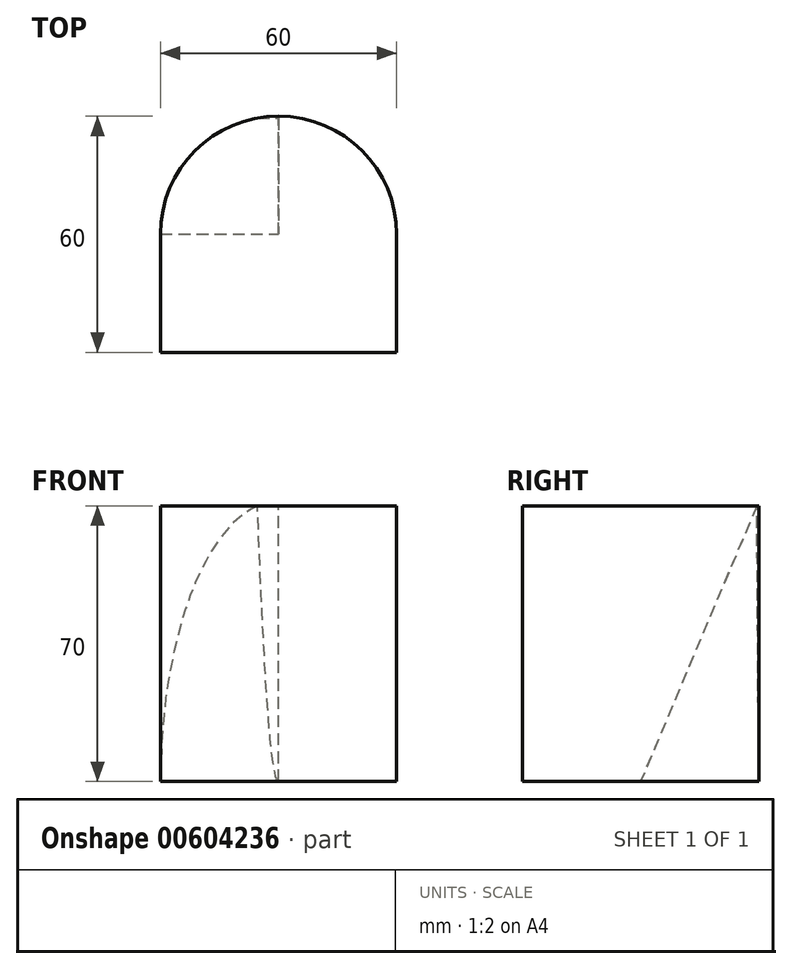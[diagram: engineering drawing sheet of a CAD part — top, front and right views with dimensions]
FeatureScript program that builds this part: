
annotation { "Feature Type Name" : "Feature", "Feature Type Description" : "" }
export const myFeature = defineFeature(function(context is Context, id is Id, definition is map)
    precondition{}
    {
        {
            var Q0;
            Q0=qCreatedBy(makeId("Top.planeOp"),FACE);
            var sketch = newSketch(context, id + "F0", { "sketchPlane" : qUnion([Q0])});
            skLineSegment(sketch, "E0.bottom", {"start": v(-30, 30) * mm, "end": v(30, 30) * mm});
            skLineSegment(sketch, "E0.top", {"start": v(-30, -30) * mm, "end": v(30, -30) * mm});
            skLineSegment(sketch, "E0.left", {"start": v(-30, 30) * mm, "end": v(-30, -30) * mm});
            skLineSegment(sketch, "E0.right", {"start": v(30, 30) * mm, "end": v(30, -30) * mm});
            skPoint(sketch, "E0.middle", {"position": v(0, 0) * mm});
            skSolve(sketch);
        }
        {
            var Q0;
            Q0=makeQuery(id+"F0.imprint","IMPRINT",FACE,{"disambiguationData":[TD([[makeQuery(id+"F0.imprint","IMPRINT",EDGE,{"derivedFrom":sQuery(id+"F0.wireOp",EDGE,"E0.bottom")}),-1.0]])]});
            extrude(context, id + "F1", {"entities" : qUnion([Q0]), "depth" : 70 * mm, "offsetDistance" : 25 * mm});
        }
        {
            var Q0;
            Q0=makeQuery(id+"F1.opExtrude","CAP_FACE",FACE,{"disambiguationData":[OSD([sQuery(id+"F0.wireOp",EDGE,"E0.bottom"),sQuery(id+"F0.wireOp",EDGE,"E0.top"),sQuery(id+"F0.wireOp",EDGE,"E0.left"),sQuery(id+"F0.wireOp",EDGE,"E0.right")])],"isStart":false});
            var sketch = newSketch(context, id + "F2", { "sketchPlane" : qUnion([Q0])});
            skCircle(sketch, "E1", {"center": v(0, 0) * mm, "radius": 30 * mm});
            skSolve(sketch);
        }
        {
            var Q0;
            {var subQ0=sQuery(id+"F2.wireOp",EDGE,"E1");var subQ1=makeQuery(id+"F1.opExtrude","CAP_EDGE",EDGE,{"disambiguationData":[OSD([sQuery(id+"F0.wireOp",EDGE,"E0.bottom")])],"isStart":false});var subQ2=makeQuery(id+"F2.imprint","INTERSECT",VERTEX,{"derivedFrom":[subQ1,subQ0]});Q0=makeQuery(id+"F2.imprint","IMPRINT",FACE,{"disambiguationData":[TD([[makeQuery(id+"F2.imprint","IMPRINT",EDGE,{"disambiguationData":[TD([[subQ2,-1.0]])],"derivedFrom":subQ0}),-1.0]])]});}
            var Q1;
            {var subQ0=sQuery(id+"F2.wireOp",EDGE,"E1");var subQ1=makeQuery(id+"F1.opExtrude","CAP_EDGE",EDGE,{"disambiguationData":[OSD([sQuery(id+"F0.wireOp",EDGE,"E0.bottom")])],"isStart":false});var subQ2=makeQuery(id+"F2.imprint","INTERSECT",VERTEX,{"derivedFrom":[subQ1,subQ0]});Q1=makeQuery(id+"F2.imprint","IMPRINT",FACE,{"disambiguationData":[TD([[makeQuery(id+"F2.imprint","IMPRINT",EDGE,{"disambiguationData":[TD([[subQ2,1.0]])],"derivedFrom":subQ0}),-1.0]])]});}
            extrude(context, id + "F3", {"entities" : qUnion([Q0, Q1]), "operationType" : NewBodyOperationType.REMOVE, "endBound" : BoundingType.THROUGH_ALL, "oppositeDirection" : true, "depth" : 25 * mm, "offsetDistance" : 25 * mm});
        }
        {
            var Q0;
            Q0=qCreatedBy(makeId("Right.planeOp"),FACE);
            var sketch = newSketch(context, id + "F4", { "sketchPlane" : qUnion([Q0])});
            skLineSegment(sketch, "E2", {"start": v(29.52, 70) * mm, "end": v(0, 0) * mm});
            skLineSegment(sketch, "E3", {"start": v(0, 0) * mm, "end": v(30, 0) * mm});
            skLineSegment(sketch, "E4", {"start": v(30, 0) * mm, "end": v(29.52, 70) * mm});
            skSolve(sketch);
        }
        {
            var Q0;
            Q0 = qSketchRegion(id + "F4", true);
            extrude(context, id + "F5", {"entities" : qUnion([Q0]), "operationType" : NewBodyOperationType.REMOVE, "endBound" : BoundingType.THROUGH_ALL, "oppositeDirection" : true, "depth" : 25 * mm, "offsetDistance" : 25 * mm});
        }
    });
